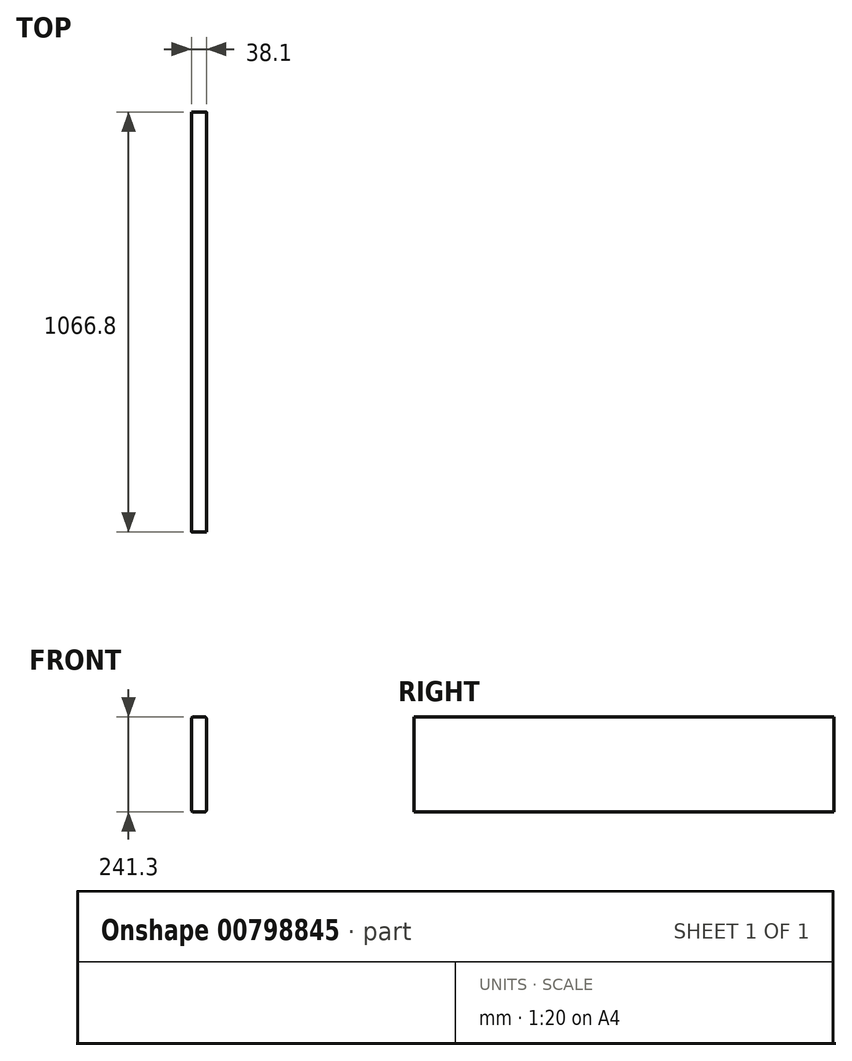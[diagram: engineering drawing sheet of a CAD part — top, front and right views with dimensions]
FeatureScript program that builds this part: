
annotation { "Feature Type Name" : "Feature", "Feature Type Description" : "" }
export const myFeature = defineFeature(function(context is Context, id is Id, definition is map)
    precondition{}
    {
        {
            var Q0;
            Q0=qCreatedBy(makeId("Front.planeOp"),FACE);
            var sketch = newSketch(context, id + "F0", { "sketchPlane" : qUnion([Q0])});
            skLineSegment(sketch, "E0.bottom", {"start": v(-14.22, 120.65) * mm, "end": v(14.22, 120.65) * mm});
            skLineSegment(sketch, "E0.top", {"start": v(-14.22, -120.65) * mm, "end": v(14.22, -120.65) * mm});
            skLineSegment(sketch, "E0.left", {"start": v(-19.05, 115.82) * mm, "end": v(-19.05, -115.82) * mm});
            skLineSegment(sketch, "E0.right", {"start": v(19.05, 115.82) * mm, "end": v(19.05, -115.82) * mm});
            skPoint(sketch, "E0.middle", {"position": v(0, 0) * mm});
            skPoint(sketch, "E1.visualSharp", {"position": v(-19.05, 120.65) * mm});
            skArc(sketch, "E1.filletArc", {"start": v(-14.22, 120.65) * mm, "mid": v(-17.64, 119.24) * mm, "end": v(-19.05, 115.82) * mm});
            skPoint(sketch, "E2.visualSharp", {"position": v(19.05, 120.65) * mm});
            skArc(sketch, "E2.filletArc", {"start": v(19.05, 115.82) * mm, "mid": v(17.64, 119.24) * mm, "end": v(14.22, 120.65) * mm});
            skPoint(sketch, "E3.visualSharp", {"position": v(19.05, -120.65) * mm});
            skArc(sketch, "E3.filletArc", {"start": v(14.22, -120.65) * mm, "mid": v(17.64, -119.24) * mm, "end": v(19.05, -115.82) * mm});
            skPoint(sketch, "E4.visualSharp", {"position": v(-19.05, -120.65) * mm});
            skArc(sketch, "E4.filletArc", {"start": v(-19.05, -115.82) * mm, "mid": v(-17.64, -119.24) * mm, "end": v(-14.22, -120.65) * mm});
            skSolve(sketch);
        }
        {
            var Q0;
            Q0=makeQuery(id+"F0.imprint","IMPRINT",FACE,{"disambiguationData":[TD([[makeQuery(id+"F0.imprint","IMPRINT",EDGE,{"derivedFrom":sQuery(id+"F0.wireOp",EDGE,"E0.bottom")}),-1.0]])]});
            extrude(context, id + "F1", {"entities" : qUnion([Q0]), "endBound" : BoundingType.SYMMETRIC, "depth" : 1066.8 * mm, "offsetDistance" : 25.4 * mm});
        }
    });
